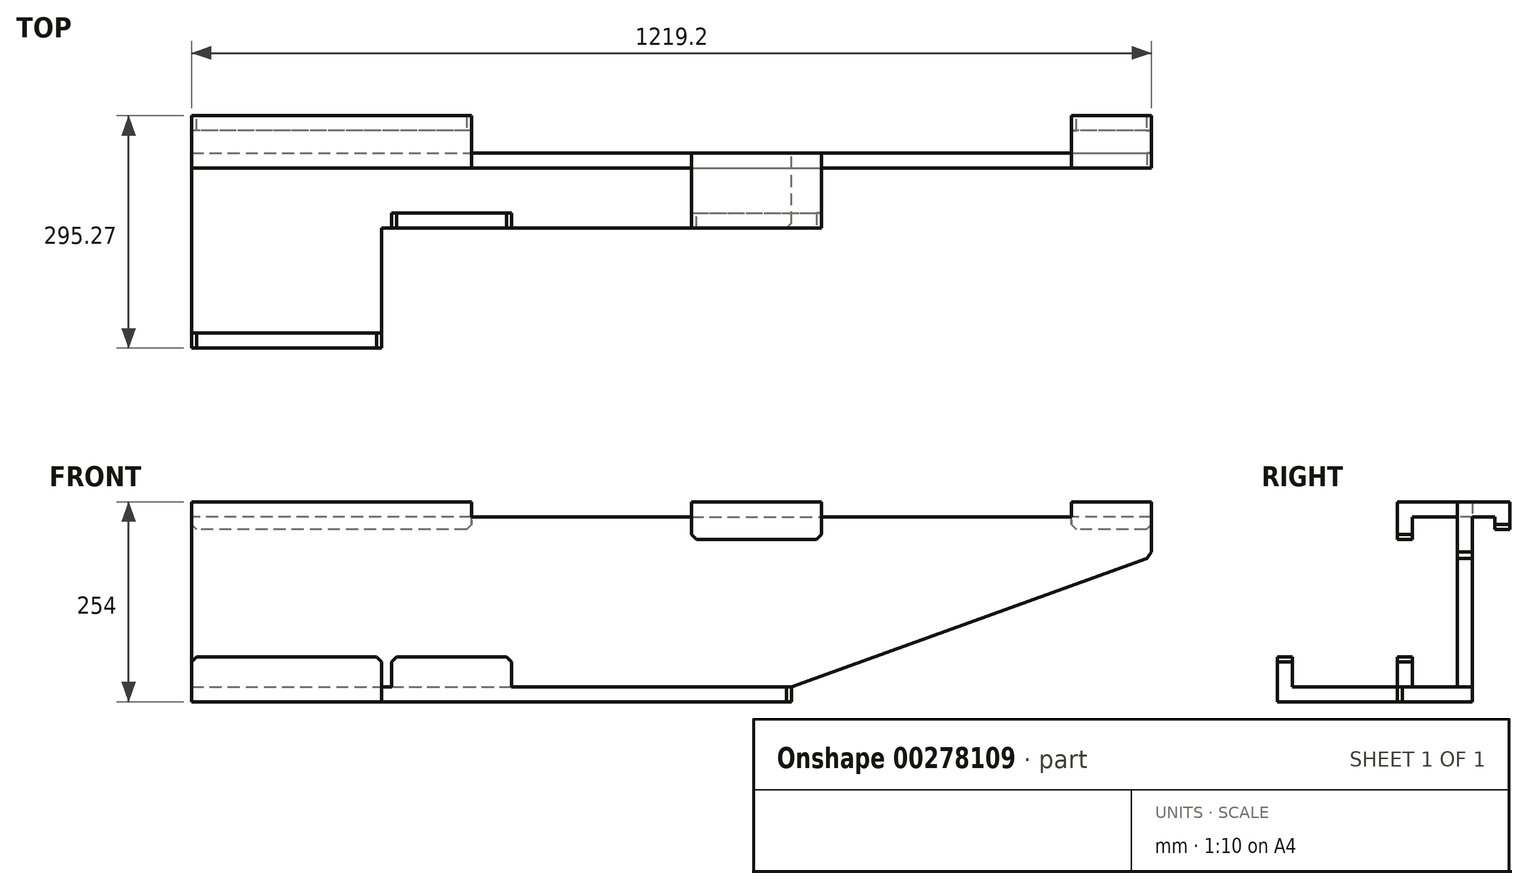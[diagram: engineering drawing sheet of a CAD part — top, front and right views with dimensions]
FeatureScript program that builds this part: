
annotation { "Feature Type Name" : "Feature", "Feature Type Description" : "" }
export const myFeature = defineFeature(function(context is Context, id is Id, definition is map)
    precondition{}
    {
        {
            var Q0;
            Q0=qCreatedBy(makeId("Front.planeOp"),FACE);
            var sketch = newSketch(context, id + "F0", { "sketchPlane" : qUnion([Q0])});
            skLineSegment(sketch, "E0.bottom", {"start": v(0, 0) * mm, "end": v(1219.2, 0) * mm});
            skLineSegment(sketch, "E0.top", {"start": v(0, -215.9) * mm, "end": v(1219.2, -215.9) * mm});
            skLineSegment(sketch, "E0.left", {"start": v(0, 0) * mm, "end": v(0, -215.9) * mm});
            skLineSegment(sketch, "E0.right", {"start": v(1219.2, 0) * mm, "end": v(1219.2, -215.9) * mm});
            skLineSegment(sketch, "E1", {"start": v(762, -215.9) * mm, "end": v(1219.2, -50.8) * mm});
            skSolve(sketch);
        }
        {
            var Q0;
            {var subQ1=sQuery(id+"F0.wireOp",EDGE,"E0.bottom");Q0=makeQuery(id+"F0.imprint","IMPRINT",FACE,{"disambiguationData":[TD([[makeQuery(id+"F0.imprint","IMPRINT",EDGE,{"derivedFrom":subQ1}),-1.0]])]});}
            extrude(context, id + "F1", {"entities" : qUnion([Q0]), "depth" : 19.05 * mm});
        }
        {
            var Q0;
            Q0=makeQuery(id+"F1.opExtrude","SWEPT_FACE",FACE,{"disambiguationData":[OSD([sQuery(id+"F0.wireOp",EDGE,"E0.bottom")])]});
            var sketch = newSketch(context, id + "F2", { "sketchPlane" : qUnion([Q0])});
            skLineSegment(sketch, "E2.bottom", {"start": v(0, -19.05) * mm, "end": v(355.6, -19.05) * mm});
            skLineSegment(sketch, "E2.top", {"start": v(0, 47.62) * mm, "end": v(355.6, 47.62) * mm});
            skLineSegment(sketch, "E2.left", {"start": v(0, -19.05) * mm, "end": v(0, 47.62) * mm});
            skLineSegment(sketch, "E2.right", {"start": v(355.6, -19.05) * mm, "end": v(355.6, 47.62) * mm});
            skLineSegment(sketch, "E3.bottom", {"start": v(1219.2, -19.05) * mm, "end": v(1117.6, -19.05) * mm});
            skLineSegment(sketch, "E3.top", {"start": v(1219.2, 47.62) * mm, "end": v(1117.6, 47.62) * mm});
            skLineSegment(sketch, "E3.left", {"start": v(1219.2, -19.05) * mm, "end": v(1219.2, 47.62) * mm});
            skLineSegment(sketch, "E3.right", {"start": v(1117.6, -19.05) * mm, "end": v(1117.6, 47.62) * mm});
            skLineSegment(sketch, "E4.bottom", {"start": v(635, 0) * mm, "end": v(647.7, 0) * mm});
            skLineSegment(sketch, "E4.top", {"start": v(635, -95.25) * mm, "end": v(800.1, -95.25) * mm});
            skLineSegment(sketch, "E4.left", {"start": v(635, 0) * mm, "end": v(635, -95.25) * mm});
            skLineSegment(sketch, "E4.right", {"start": v(800.1, 0) * mm, "end": v(800.1, -95.25) * mm});
            skSolve(sketch);
        }
        {
            var Q0;
            Q0 = qSketchRegion(id + "F2", true);
            var Q1;
            {var subQ0=sQuery(id+"F2.wireOp",EDGE,"E4.top");Q1=makeQuery(id+"F2.imprint","IMPRINT",FACE,{"disambiguationData":[TD([[makeQuery(id+"F2.imprint","IMPRINT",EDGE,{"derivedFrom":subQ0}),1.0]])]});}
            var Q2;
            {var subQ0=sQuery(id+"F2.wireOp",EDGE,"E4.bottom");Q2=makeQuery(id+"F2.imprint","IMPRINT",FACE,{"disambiguationData":[TD([[makeQuery(id+"F2.imprint","IMPRINT",EDGE,{"derivedFrom":subQ0}),-1.0]])]});}
            extrude(context, id + "F3", {"entities" : qUnion([Q0, Q1, Q2]), "operationType" : NewBodyOperationType.ADD, "depth" : 19.05 * mm});
        }
        {
            var Q0;
            Q0=makeQuery(id+"F1.opExtrude","SWEPT_FACE",FACE,{"disambiguationData":[OSD([sQuery(id+"F0.wireOp",EDGE,"E0.bottom")])]});
            var sketch = newSketch(context, id + "F4", { "sketchPlane" : qUnion([Q0])});
            skLineSegment(sketch, "E5.bottom", {"start": v(1219.2, 47.62) * mm, "end": v(1117.6, 47.62) * mm});
            skLineSegment(sketch, "E5.top", {"start": v(1219.2, 28.57) * mm, "end": v(1117.6, 28.57) * mm});
            skLineSegment(sketch, "E5.left", {"start": v(1219.2, 47.62) * mm, "end": v(1219.2, 28.57) * mm});
            skLineSegment(sketch, "E5.right", {"start": v(1117.6, 47.62) * mm, "end": v(1117.6, 28.57) * mm});
            skLineSegment(sketch, "E6.bottom", {"start": v(355.6, 47.62) * mm, "end": v(0, 47.62) * mm});
            skLineSegment(sketch, "E6.top", {"start": v(355.6, 28.57) * mm, "end": v(0, 28.57) * mm});
            skLineSegment(sketch, "E6.left", {"start": v(355.6, 47.62) * mm, "end": v(355.6, 28.57) * mm});
            skLineSegment(sketch, "E6.right", {"start": v(0, 47.62) * mm, "end": v(0, 28.57) * mm});
            skLineSegment(sketch, "E7.bottom", {"start": v(635, -95.25) * mm, "end": v(800.1, -95.25) * mm});
            skLineSegment(sketch, "E7.top", {"start": v(635, -76.2) * mm, "end": v(800.1, -76.2) * mm});
            skLineSegment(sketch, "E7.left", {"start": v(635, -95.25) * mm, "end": v(635, -76.2) * mm});
            skLineSegment(sketch, "E7.right", {"start": v(800.1, -95.25) * mm, "end": v(800.1, -76.2) * mm});
            skSolve(sketch);
        }
        {
            var Q0;
            Q0 = qSketchRegion(id + "F4", true);
            extrude(context, id + "F5", {"entities" : qUnion([Q0]), "operationType" : NewBodyOperationType.ADD, "oppositeDirection" : true, "depth" : 15.88 * mm});
        }
        {
            var Q0;
            Q0=makeQuery(id+"F1.opExtrude","SWEPT_FACE",FACE,{"disambiguationData":[OSD([sQuery(id+"F0.wireOp",EDGE,"E0.top")])]});
            var sketch = newSketch(context, id + "F6", { "sketchPlane" : qUnion([Q0])});
            skLineSegment(sketch, "E8.bottom", {"start": v(0, 0) * mm, "end": v(762, 0) * mm});
            skLineSegment(sketch, "E8.top", {"start": v(0, 95.25) * mm, "end": v(762, 95.25) * mm});
            skLineSegment(sketch, "E8.left", {"start": v(0, 0) * mm, "end": v(0, 95.25) * mm});
            skLineSegment(sketch, "E8.right", {"start": v(762, 0) * mm, "end": v(762, 95.25) * mm});
            skLineSegment(sketch, "E9", {"start": v(0, 95.25) * mm, "end": v(0, 247.65) * mm});
            skLineSegment(sketch, "E10", {"start": v(0, 247.65) * mm, "end": v(241.3, 247.65) * mm});
            skLineSegment(sketch, "E11", {"start": v(241.3, 247.65) * mm, "end": v(241.3, 95.25) * mm});
            skSolve(sketch);
        }
        {
            var Q0;
            Q0 = qSketchRegion(id + "F6", true);
            extrude(context, id + "F7", {"entities" : qUnion([Q0]), "operationType" : NewBodyOperationType.ADD, "depth" : 19.05 * mm});
        }
        {
            var Q0;
            Q0=makeQuery(id+"F7.opExtrude","CAP_FACE",FACE,{"disambiguationData":[OSD([sQuery(id+"F6.wireOp",EDGE,"E8.bottom"),sQuery(id+"F6.wireOp",EDGE,"E8.top"),sQuery(id+"F6.wireOp",EDGE,"E8.left"),sQuery(id+"F6.wireOp",EDGE,"E8.right")])],"isStart":true});
            var sketch = newSketch(context, id + "F8", { "sketchPlane" : qUnion([Q0])});
            skLineSegment(sketch, "E12.bottom", {"start": v(406.4, -95.25) * mm, "end": v(762, -95.25) * mm});
            skLineSegment(sketch, "E12.top", {"start": v(254, -76.2) * mm, "end": v(406.4, -76.2) * mm});
            skLineSegment(sketch, "E12.left", {"start": v(254, -95.25) * mm, "end": v(254, -76.2) * mm});
            skLineSegment(sketch, "E13", {"start": v(406.4, -76.2) * mm, "end": v(406.4, -95.25) * mm});
            skLineSegment(sketch, "E14.bottom", {"start": v(0, -247.65) * mm, "end": v(241.3, -247.65) * mm});
            skLineSegment(sketch, "E14.top", {"start": v(0, -228.6) * mm, "end": v(241.3, -228.6) * mm});
            skLineSegment(sketch, "E14.left", {"start": v(0, -247.65) * mm, "end": v(0, -228.6) * mm});
            skLineSegment(sketch, "E14.right", {"start": v(241.3, -247.65) * mm, "end": v(241.3, -228.6) * mm});
            skSolve(sketch);
        }
        {
            var Q0;
            Q0 = qSketchRegion(id + "F8", true);
            var Q1;
            Q1=makeQuery(id+"F8.imprint","IMPRINT",FACE,{"disambiguationData":[TD([[makeQuery(id+"F8.imprint","IMPRINT",EDGE,{"derivedFrom":sQuery(id+"F8.wireOp",EDGE,"E12.top")}),-1.0]])]});
            extrude(context, id + "F9", {"entities" : qUnion([Q0, Q1]), "operationType" : NewBodyOperationType.ADD, "depth" : 38.1 * mm});
        }
        {
            var Q0;
            Q0=makeQuery(id+"F5.opExtrude","CAP_FACE",FACE,{"disambiguationData":[OSD([sQuery(id+"F4.wireOp",EDGE,"E7.bottom"),sQuery(id+"F4.wireOp",EDGE,"E7.top"),sQuery(id+"F4.wireOp",EDGE,"E7.left"),sQuery(id+"F4.wireOp",EDGE,"E7.right")])],"isStart":false});
            extrude(context, id + "F10", {"entities" : qUnion([Q0]), "operationType" : NewBodyOperationType.ADD, "depth" : 12.7 * mm});
        }
        {
            var Q0;
            Q0=makeQuery(id+"F9.opExtrude","CAP_EDGE",EDGE,{"disambiguationData":[OSD([sQuery(id+"F8.wireOp",EDGE,"E14.left")])],"isStart":false});
            var Q1;
            Q1=makeQuery(id+"F9.opExtrude","CAP_EDGE",EDGE,{"disambiguationData":[OSD([sQuery(id+"F8.wireOp",EDGE,"E14.right")])],"isStart":false});
            var Q2;
            Q2=makeQuery(id+"F9.opExtrude","CAP_EDGE",EDGE,{"disambiguationData":[OSD([sQuery(id+"F8.wireOp",EDGE,"E12.left")])],"isStart":false});
            var Q3;
            Q3=makeQuery(id+"F9.opExtrude","CAP_EDGE",EDGE,{"disambiguationData":[OSD([sQuery(id+"F8.wireOp",EDGE,"E13")])],"isStart":false});
            var Q4;
            Q4=makeQuery(id+"F10.opExtrude","CAP_EDGE",EDGE,{"disambiguationData":[OSD([sQuery(id+"F4.wireOp",EDGE,"E7.right")])],"isStart":false});
            var Q5;
            Q5=makeQuery(id+"F10.opExtrude","CAP_EDGE",EDGE,{"disambiguationData":[OSD([sQuery(id+"F4.wireOp",EDGE,"E7.left")])],"isStart":false});
            var Q6;
            Q6=makeQuery(id+"F7.opExtrude","SWEPT_EDGE",EDGE,{"disambiguationData":[OSD([sQuery(id+"F6.wireOp",EDGE,"E8.top"),sQuery(id+"F6.wireOp",EDGE,"E8.right")])]});
            var Q7;
            Q7=makeQuery(id+"F1.opExtrude","SWEPT_EDGE",EDGE,{"disambiguationData":[OSD([sQuery(id+"F0.wireOp",EDGE,"E0.right"),sQuery(id+"F0.wireOp",EDGE,"655zPpD2-Q9yU-ipV1-fvyL-oAU6hB0cfrad")])]});
            var Q8;
            Q8=makeQuery(id+"F5.opExtrude","CAP_EDGE",EDGE,{"disambiguationData":[OSD([sQuery(id+"F4.wireOp",EDGE,"E5.left")])],"isStart":false});
            var Q9;
            Q9=makeQuery(id+"F5.opExtrude","CAP_EDGE",EDGE,{"disambiguationData":[OSD([sQuery(id+"F4.wireOp",EDGE,"E6.left")])],"isStart":false});
            var Q10;
            Q10=makeQuery(id+"F5.opExtrude","CAP_EDGE",EDGE,{"disambiguationData":[OSD([sQuery(id+"F4.wireOp",EDGE,"E5.right")])],"isStart":false});
            var Q11;
            Q11=makeQuery(id+"F5.opExtrude","CAP_EDGE",EDGE,{"disambiguationData":[OSD([sQuery(id+"F4.wireOp",EDGE,"E6.right")])],"isStart":false});
            chamfer(context, id + "F11", {"entities" : qUnion([Q0, Q1, Q2, Q3, Q4, Q5, Q6, Q7, Q8, Q9, Q10, Q11]), "width" : 6.35 * mm, "tangentPropagation" : true});
        }
    });
